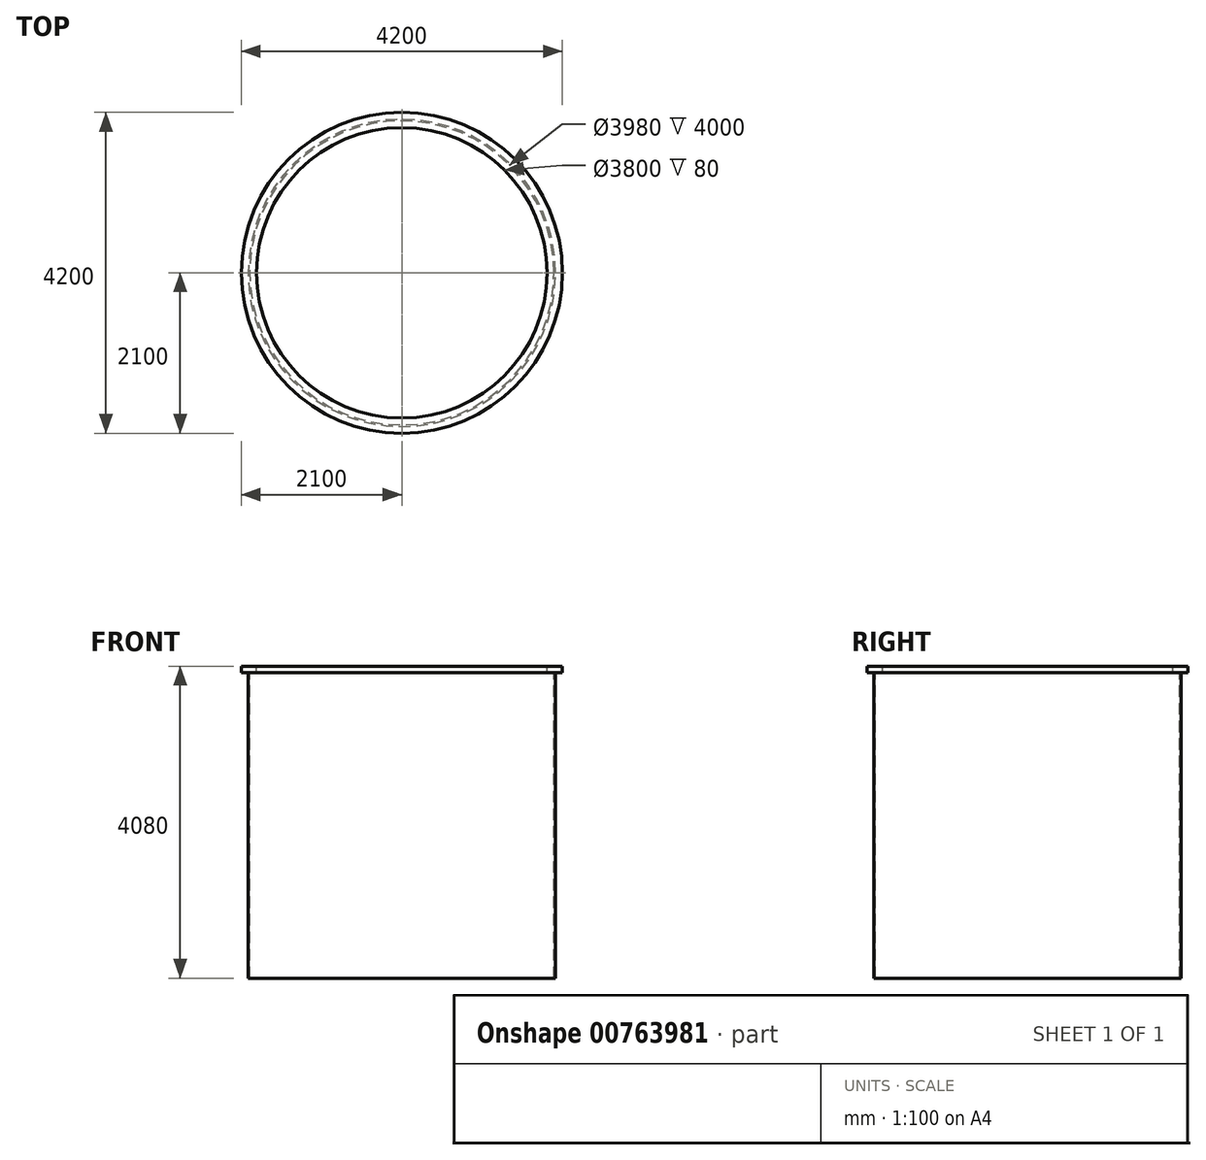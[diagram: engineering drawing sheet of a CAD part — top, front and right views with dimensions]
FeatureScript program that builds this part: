
annotation { "Feature Type Name" : "Feature", "Feature Type Description" : "" }
export const myFeature = defineFeature(function(context is Context, id is Id, definition is map)
    precondition{}
    {
        {
            var Q0;
            Q0=qCreatedBy(makeId("Front.planeOp"),FACE);
            var sketch = newSketch(context, id + "F0", { "sketchPlane" : qUnion([Q0])});
            skLineSegment(sketch, "E0.bottom", {"start": v(-2010, 0) * mm, "end": v(-1990, 0) * mm});
            skLineSegment(sketch, "E0.top", {"start": v(-2010, -4000) * mm, "end": v(-1990, -4000) * mm});
            skLineSegment(sketch, "E0.left", {"start": v(-2010, 0) * mm, "end": v(-2010, -4000) * mm});
            skLineSegment(sketch, "E0.right", {"start": v(-1990, 0) * mm, "end": v(-1990, -4000) * mm});
            skLineSegment(sketch, "E1.bottom", {"start": v(-1900, 0) * mm, "end": v(-2100, 0) * mm});
            skLineSegment(sketch, "E1.top", {"start": v(-1900, 80) * mm, "end": v(-2100, 80) * mm});
            skLineSegment(sketch, "E1.left", {"start": v(-1900, 0) * mm, "end": v(-1900, 80) * mm});
            skLineSegment(sketch, "E1.right", {"start": v(-2100, 0) * mm, "end": v(-2100, 80) * mm});
            skPoint(sketch, "E2", {"position": v(-2000, -4000) * mm});
            skLineSegment(sketch, "E3", {"start": v(0, 0) * mm, "end": v(0, -500) * mm, "construction": true});
            skSolve(sketch);
        }
        {
            var Q0;
            Q0=makeQuery(id+"F0.imprint","IMPRINT",FACE,{"disambiguationData":[TD([[makeQuery(id+"F0.imprint","IMPRINT",EDGE,{"derivedFrom":sQuery(id+"F0.wireOp",EDGE,"E1.top")}),1.0]])]});
            var Q1;
            Q1=sQuery(id+"F0.wireOp",EDGE,"E3");
            revolve(context, id + "F1", {"surfaceOperationType" : NewSurfaceOperationType.NEW, "entities" : qUnion([Q0]), "axis" : qUnion([Q1]), "revolveType" : RevolveType.FULL});
        }
        {
            var Q0;
            Q0=makeQuery(id+"F0.imprint","IMPRINT",FACE,{"disambiguationData":[TD([[makeQuery(id+"F0.imprint","IMPRINT",EDGE,{"derivedFrom":sQuery(id+"F0.wireOp",EDGE,"E0.top")}),1.0]])]});
            var Q1;
            Q1=sQuery(id+"F0.wireOp",EDGE,"E3");
            revolve(context, id + "F2", {"surfaceOperationType" : NewSurfaceOperationType.NEW, "entities" : qUnion([Q0]), "axis" : qUnion([Q1]), "revolveType" : RevolveType.FULL});
        }
    });
